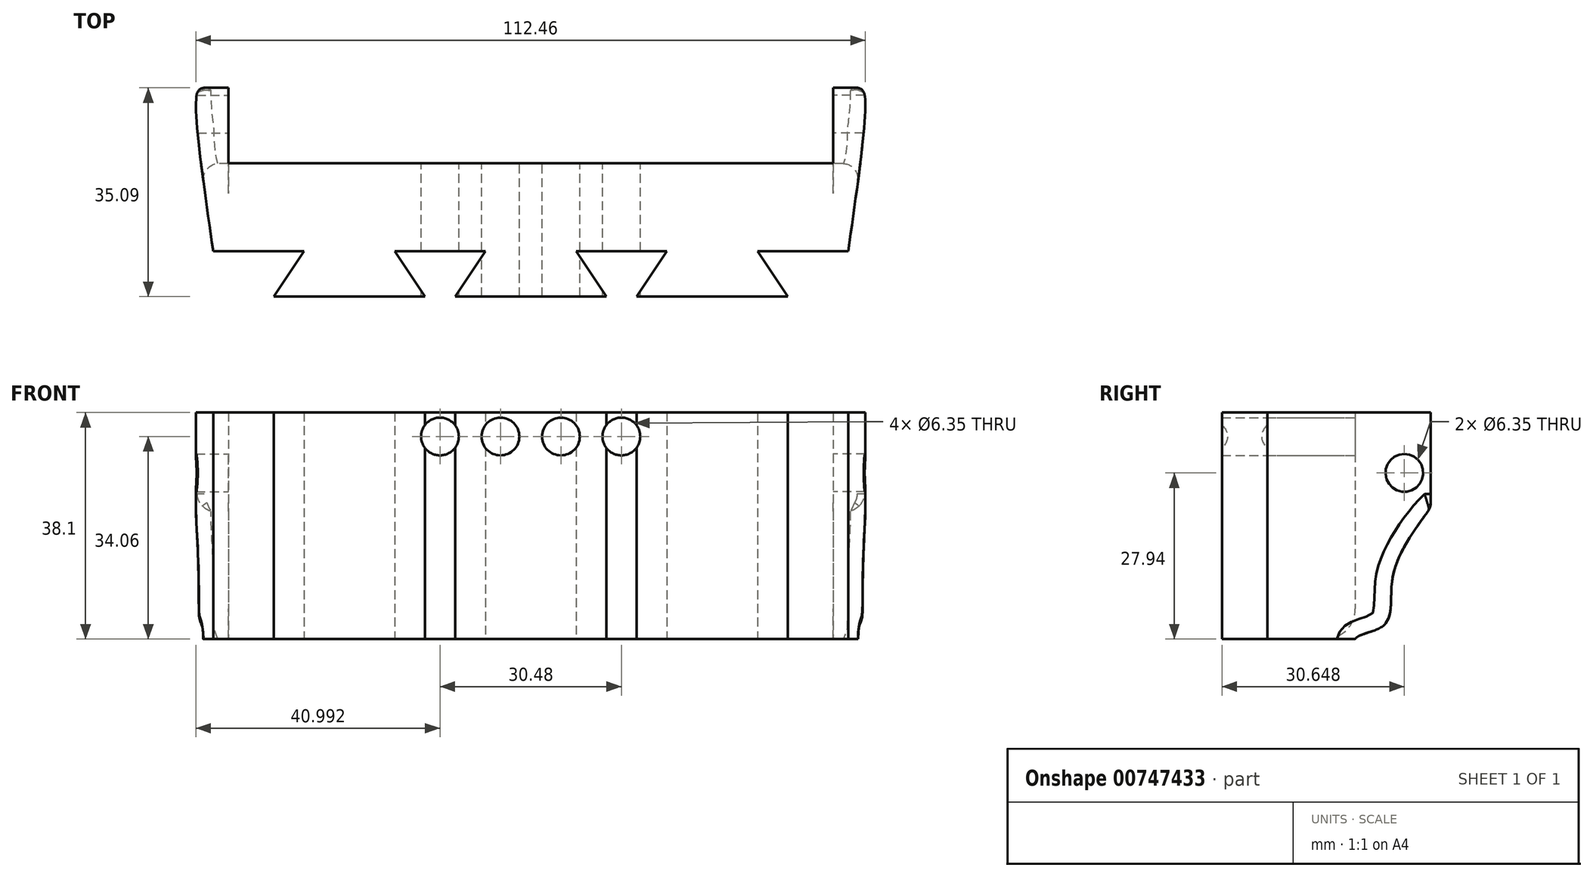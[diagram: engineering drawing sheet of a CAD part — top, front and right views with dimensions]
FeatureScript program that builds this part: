
annotation { "Feature Type Name" : "Feature", "Feature Type Description" : "" }
export const myFeature = defineFeature(function(context is Context, id is Id, definition is map)
    precondition{}
    {
        {
            var Q0;
            Q0=qCreatedBy(makeId("Top.planeOp"),FACE);
            var sketch = newSketch(context, id + "F0", { "sketchPlane" : qUnion([Q0])});
            skLineSegment(sketch, "E0.bottom", {"start": v(-93.77, 17.84) * mm, "end": v(-78.53, 17.84) * mm});
            skLineSegment(sketch, "E1", {"start": v(-78.53, 17.84) * mm, "end": v(-83.6, 10.22) * mm});
            skLineSegment(sketch, "E2", {"start": v(-83.6, 10.22) * mm, "end": v(-58.2, 10.22) * mm});
            skLineSegment(sketch, "E3", {"start": v(-58.2, 10.22) * mm, "end": v(-63.29, 17.84) * mm});
            skLineSegment(sketch, "E4", {"start": v(-48.05, 17.84) * mm, "end": v(-53.13, 10.22) * mm});
            skLineSegment(sketch, "E5", {"start": v(-53.13, 10.22) * mm, "end": v(-27.73, 10.22) * mm});
            skLineSegment(sketch, "E6", {"start": v(-27.73, 10.22) * mm, "end": v(-32.8, 17.84) * mm});
            skLineSegment(sketch, "E7", {"start": v(-17.57, 17.84) * mm, "end": v(-22.65, 10.22) * mm});
            skLineSegment(sketch, "E8", {"start": v(-22.65, 10.22) * mm, "end": v(2.75, 10.22) * mm});
            skLineSegment(sketch, "E9", {"start": v(2.75, 10.22) * mm, "end": v(-2.33, 17.84) * mm});
            skLineSegment(sketch, "E10.trimOffspring", {"start": v(-63.29, 17.84) * mm, "end": v(-48.05, 17.84) * mm});
            skLineSegment(sketch, "E11.trimOffspring", {"start": v(-32.8, 17.84) * mm, "end": v(-17.57, 17.84) * mm});
            skLineSegment(sketch, "E12.trimOffspring", {"start": v(-2.33, 17.84) * mm, "end": v(12.91, 17.84) * mm});
            skLineSegment(sketch, "E13.top", {"start": v(-93.77, 45.31) * mm, "end": v(-91.23, 45.31) * mm});
            skLineSegment(sketch, "E14.top", {"start": v(-91.23, 32.61) * mm, "end": v(10.37, 32.61) * mm});
            skLineSegment(sketch, "E14.left", {"start": v(-91.23, 45.31) * mm, "end": v(-91.23, 32.61) * mm});
            skLineSegment(sketch, "E14.right", {"start": v(10.37, 45.31) * mm, "end": v(10.37, 32.61) * mm});
            skLineSegment(sketch, "E15.trimOffspring", {"start": v(10.37, 45.31) * mm, "end": v(12.91, 45.31) * mm});
            skFitSpline(sketch, "E16", {"points": [v(-93.77, 17.84) * mm, v(-96.65, 42.8) * mm, v(-96.3, 45.31) * mm], "startDerivative": vector(-5.5, 38.08) * mm, "endDerivative": vector(1.13, 7.61) * mm});
            skLineSegment(sketch, "E17", {"start": v(-96.3, 45.31) * mm, "end": v(-93.77, 45.31) * mm});
            skLineSegment(sketch, "E18.MirrorCS", {"start": v(15.45, 45.31) * mm, "end": v(12.91, 45.31) * mm});
            skFitSpline(sketch, "E19.MirrorCS", {"points": [v(12.91, 17.84) * mm, v(15.8, 42.8) * mm, v(15.45, 45.31) * mm], "startDerivative": vector(5.5, 38.08) * mm, "endDerivative": vector(-1.13, 7.61) * mm});
            skPoint(sketch, "E20.start.orphan", {"position": v(-40.43, 32.61) * mm});
            skSolve(sketch);
        }
        {
            var Q0;
            Q0=makeQuery(id+"F0.imprint","IMPRINT",FACE,{"disambiguationData":[TD([[makeQuery(id+"F0.imprint","IMPRINT",EDGE,{"derivedFrom":sQuery(id+"F0.wireOp",EDGE,"E1")}),1.0]])]});
            extrude(context, id + "F1", {"entities" : qUnion([Q0]), "depth" : 38.1 * mm, "offsetDistance" : 25.4 * mm});
        }
        {
            var Q0;
            Q0=makeQuery(id+"F1.opExtrude","SWEPT_FACE",FACE,{"disambiguationData":[OSD([sQuery(id+"F0.wireOp",EDGE,"E14.top")])]});
            var sketch = newSketch(context, id + "F2", { "sketchPlane" : qUnion([Q0])});
            skPoint(sketch, "E21", {"position": v(25.19, 34.06) * mm});
            skPoint(sketch, "E22", {"position": v(35.35, 34.06) * mm});
            skPoint(sketch, "E23", {"position": v(45.5, 34.06) * mm});
            skPoint(sketch, "E24", {"position": v(55.67, 34.06) * mm});
            skPoint(sketch, "E25.end.orphan", {"position": v(40.43, 38.1) * mm});
            skPoint(sketch, "E25.start.orphan", {"position": v(40.43, 0) * mm});
            skSolve(sketch);
        }
        {
            var Q0;
            Q0=sQuery(id+"F2.wireOp",VERTEX,"E21");
            var Q1;
            Q1=sQuery(id+"F2.wireOp",VERTEX,"E22");
            var Q2;
            Q2=sQuery(id+"F2.wireOp",VERTEX,"E23");
            var Q3;
            Q3=sQuery(id+"F2.wireOp",VERTEX,"E24");
            var Q4;
            Q4=makeQuery(id+"F1.opExtrude","SWEPT_BODY",BODY,{"disambiguationData":[OSD([sQuery(id+"F0.wireOp",EDGE,"E1"),sQuery(id+"F0.wireOp",EDGE,"E2"),sQuery(id+"F0.wireOp",EDGE,"E3"),sQuery(id+"F0.wireOp",EDGE,"E4"),sQuery(id+"F0.wireOp",EDGE,"E5"),sQuery(id+"F0.wireOp",EDGE,"E6"),sQuery(id+"F0.wireOp",EDGE,"E7"),sQuery(id+"F0.wireOp",EDGE,"E8"),sQuery(id+"F0.wireOp",EDGE,"E9"),sQuery(id+"F0.wireOp",EDGE,"E0.bottom"),sQuery(id+"F0.wireOp",EDGE,"E13.top"),sQuery(id+"F0.wireOp",EDGE,"E10.trimOffspring"),sQuery(id+"F0.wireOp",EDGE,"E12.trimOffspring"),sQuery(id+"F0.wireOp",EDGE,"E11.trimOffspring"),sQuery(id+"F0.wireOp",EDGE,"E14.top"),sQuery(id+"F0.wireOp",EDGE,"E14.left"),sQuery(id+"F0.wireOp",EDGE,"E14.right"),sQuery(id+"F0.wireOp",EDGE,"E15.trimOffspring"),sQuery(id+"F0.wireOp",EDGE,"E16"),sQuery(id+"F0.wireOp",EDGE,"E17"),sQuery(id+"F0.wireOp",EDGE,"99fc5418-5779-44d2-9f62-ac1456794f190.MirrorCS"),sQuery(id+"F0.wireOp",EDGE,"E18.MirrorCS")])]});
            hole(context, id + "F3", {"style" : HoleStyle.SIMPLE, "endStyle" : HoleEndStyle.BLIND, "holeDiameter" : 6.35 * mm, "majorDiameter" : 6.35 * mm, "holeDepth" : 203.2 * mm, "isTappedThrough" : true, "tappedDepth" : 12.7 * mm, "tapClearance" : 3, "locations" : qUnion([Q0, Q1, Q2, Q3]), "scope" : qUnion([Q4])});
        }
        {
            var Q0;
            Q0=makeQuery(id+"F1.opExtrude","SWEPT_FACE",FACE,{"disambiguationData":[OSD([sQuery(id+"F0.wireOp",EDGE,"E14.right")])]});
            var sketch = newSketch(context, id + "F4", { "sketchPlane" : qUnion([Q0])});
            skPoint(sketch, "E26", {"position": v(-40.87, 27.94) * mm});
            skLineSegment(sketch, "E27", {"start": v(-32.61, 38.1) * mm, "end": v(-45.31, 38.1) * mm});
            skCircle(sketch, "E28", {"center": v(-40.87, 27.94) * mm, "radius": 3.18 * mm});
            skLineSegment(sketch, "E29", {"start": v(-32.61, 38.1) * mm, "end": v(-32.61, 26.15) * mm});
            skSolve(sketch);
        }
        {
            var Q0;
            Q0=sQuery(id+"F4.wireOp",VERTEX,"E26");
            var Q1;
            Q1=makeQuery(id+"F1.opExtrude","SWEPT_BODY",BODY,{"disambiguationData":[OSD([sQuery(id+"F0.wireOp",EDGE,"E1"),sQuery(id+"F0.wireOp",EDGE,"E2"),sQuery(id+"F0.wireOp",EDGE,"E3"),sQuery(id+"F0.wireOp",EDGE,"E4"),sQuery(id+"F0.wireOp",EDGE,"E5"),sQuery(id+"F0.wireOp",EDGE,"E6"),sQuery(id+"F0.wireOp",EDGE,"E7"),sQuery(id+"F0.wireOp",EDGE,"E8"),sQuery(id+"F0.wireOp",EDGE,"E9"),sQuery(id+"F0.wireOp",EDGE,"E0.bottom"),sQuery(id+"F0.wireOp",EDGE,"E13.top"),sQuery(id+"F0.wireOp",EDGE,"E10.trimOffspring"),sQuery(id+"F0.wireOp",EDGE,"E12.trimOffspring"),sQuery(id+"F0.wireOp",EDGE,"E11.trimOffspring"),sQuery(id+"F0.wireOp",EDGE,"E14.top"),sQuery(id+"F0.wireOp",EDGE,"E14.left"),sQuery(id+"F0.wireOp",EDGE,"E14.right"),sQuery(id+"F0.wireOp",EDGE,"E15.trimOffspring"),sQuery(id+"F0.wireOp",EDGE,"E16"),sQuery(id+"F0.wireOp",EDGE,"E17"),sQuery(id+"F0.wireOp",EDGE,"99fc5418-5779-44d2-9f62-ac1456794f190.MirrorCS"),sQuery(id+"F0.wireOp",EDGE,"E18.MirrorCS")])]});
            hole(context, id + "F5", {"style" : HoleStyle.SIMPLE, "endStyle" : HoleEndStyle.THROUGH, "holeDiameter" : 6.35 * mm, "majorDiameter" : 6.35 * mm, "isTappedThrough" : true, "tappedDepth" : 12.7 * mm, "tapClearance" : 3, "locations" : qUnion([Q0]), "scope" : qUnion([Q1])});
        }
        {
            var Q0;
            Q0=sQuery(id+"F4.wireOp",VERTEX,"E26");
            var Q1;
            Q1=makeQuery(id+"F1.opExtrude","SWEPT_BODY",BODY,{"disambiguationData":[OSD([sQuery(id+"F0.wireOp",EDGE,"E1"),sQuery(id+"F0.wireOp",EDGE,"E2"),sQuery(id+"F0.wireOp",EDGE,"E3"),sQuery(id+"F0.wireOp",EDGE,"E4"),sQuery(id+"F0.wireOp",EDGE,"E5"),sQuery(id+"F0.wireOp",EDGE,"E6"),sQuery(id+"F0.wireOp",EDGE,"E7"),sQuery(id+"F0.wireOp",EDGE,"E8"),sQuery(id+"F0.wireOp",EDGE,"E9"),sQuery(id+"F0.wireOp",EDGE,"E0.bottom"),sQuery(id+"F0.wireOp",EDGE,"E13.top"),sQuery(id+"F0.wireOp",EDGE,"E10.trimOffspring"),sQuery(id+"F0.wireOp",EDGE,"E12.trimOffspring"),sQuery(id+"F0.wireOp",EDGE,"E11.trimOffspring"),sQuery(id+"F0.wireOp",EDGE,"E14.top"),sQuery(id+"F0.wireOp",EDGE,"E14.left"),sQuery(id+"F0.wireOp",EDGE,"E14.right"),sQuery(id+"F0.wireOp",EDGE,"E15.trimOffspring"),sQuery(id+"F0.wireOp",EDGE,"E16"),sQuery(id+"F0.wireOp",EDGE,"E17"),sQuery(id+"F0.wireOp",EDGE,"99fc5418-5779-44d2-9f62-ac1456794f190.MirrorCS"),sQuery(id+"F0.wireOp",EDGE,"E18.MirrorCS")])]});
            hole(context, id + "F6", {"style" : HoleStyle.SIMPLE, "endStyle" : HoleEndStyle.THROUGH, "oppositeDirection" : true, "holeDiameter" : 6.35 * mm, "majorDiameter" : 6.35 * mm, "isTappedThrough" : true, "tappedDepth" : 12.7 * mm, "tapClearance" : 3, "locations" : qUnion([Q0]), "scope" : qUnion([Q1])});
        }
        {
            var Q0;
            Q0=makeQuery(id+"F1.opExtrude","CAP_EDGE",EDGE,{"disambiguationData":[OSD([sQuery(id+"F0.wireOp",EDGE,"E14.top")])],"isStart":true});
            fillet(context, id + "F7", {"entities" : qUnion([Q0]), "radius" : 5.08 * mm, "tangentPropagation" : true, "allowEdgeOverflow" : false});
        }
        {
            var Q0;
            Q0=makeQuery(id+"F1.opExtrude","SWEPT_EDGE",EDGE,{"disambiguationData":[OSD([sQuery(id+"F0.wireOp",EDGE,"E16"),sQuery(id+"F0.wireOp",EDGE,"E17")])]});
            var Q1;
            Q1=makeQuery(id+"F1.opExtrude","SWEPT_EDGE",EDGE,{"disambiguationData":[OSD([sQuery(id+"F0.wireOp",EDGE,"99fc5418-5779-44d2-9f62-ac1456794f190.MirrorCS"),sQuery(id+"F0.wireOp",EDGE,"E18.MirrorCS")])]});
            fillet(context, id + "F8", {"entities" : qUnion([Q0, Q1]), "radius" : 1.27 * mm, "tangentPropagation" : true, "allowEdgeOverflow" : false});
        }
        {
            var Q0;
            Q0=qCreatedBy(makeId("Right.planeOp"),FACE);
            var sketch = newSketch(context, id + "F9", { "sketchPlane" : qUnion([Q0])});
            skFitSpline(sketch, "E30", {"points": [v(45.8, 22.78) * mm, v(38.88, 10.27) * mm, v(37.56, 2.43) * mm, v(32.57, 0) * mm, v(34.1, -4.08) * mm], "startDerivative": vector(-27.14, -36.39) * mm, "endDerivative": vector(17.27, -25.25) * mm});
            skLineSegment(sketch, "E31", {"start": v(45.8, 22.78) * mm, "end": v(45.8, -5.1) * mm});
            skLineSegment(sketch, "E32", {"start": v(45.8, -5.1) * mm, "end": v(34.1, -4.08) * mm});
            skSolve(sketch);
        }
        {
            var Q0;
            Q0=makeQuery(id+"F9.imprint","IMPRINT",FACE,{"disambiguationData":[TD([[makeQuery(id+"F9.imprint","IMPRINT",EDGE,{"derivedFrom":sQuery(id+"F9.wireOp",EDGE,"E30")}),1.0]])]});
            extrude(context, id + "F10", {"entities" : qUnion([Q0]), "operationType" : NewBodyOperationType.REMOVE, "endBound" : BoundingType.SYMMETRIC, "depth" : 2032 * mm, "offsetDistance" : 25.4 * mm});
        }
        {
            var Q0;
            Q0=makeQuery(id+"F10.boolean.opBoolean","INTERSECT",EDGE,{"derivedFrom":[makeQuery(id+"F1.opExtrude","SWEPT_FACE",FACE,{"disambiguationData":[OSD([sQuery(id+"F0.wireOp",EDGE,"E15.trimOffspring"),sQuery(id+"F0.wireOp",EDGE,"E18.MirrorCS")])]}),makeQuery(id+"F10.opExtrude","SWEPT_FACE",FACE,{"disambiguationData":[OSD([sQuery(id+"F9.wireOp",EDGE,"E30")])]})]});
            var Q1;
            Q1=makeQuery(id+"F10.boolean.opBoolean","INTERSECT",EDGE,{"derivedFrom":[makeQuery(id+"F1.opExtrude","SWEPT_FACE",FACE,{"disambiguationData":[OSD([sQuery(id+"F0.wireOp",EDGE,"E13.top"),sQuery(id+"F0.wireOp",EDGE,"E17")])]}),makeQuery(id+"F10.opExtrude","SWEPT_FACE",FACE,{"disambiguationData":[OSD([sQuery(id+"F9.wireOp",EDGE,"E30")])]})]});
            fillet(context, id + "F11", {"entities" : qUnion([Q0, Q1]), "radius" : 2.54 * mm, "tangentPropagation" : true, "allowEdgeOverflow" : false});
        }
    });
